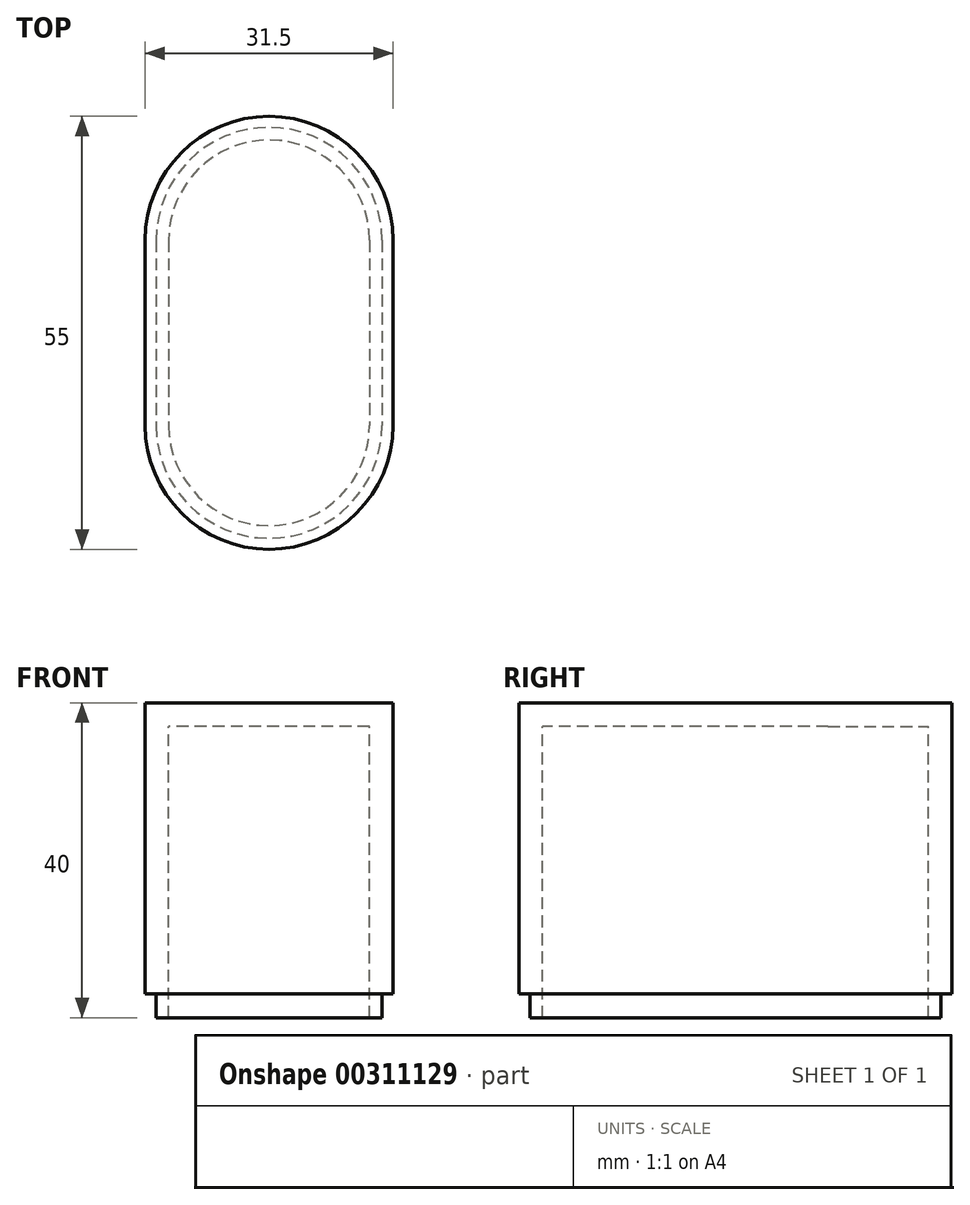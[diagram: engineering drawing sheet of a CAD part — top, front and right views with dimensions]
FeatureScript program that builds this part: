
annotation { "Feature Type Name" : "Feature", "Feature Type Description" : "" }
export const myFeature = defineFeature(function(context is Context, id is Id, definition is map)
    precondition{}
    {
        {
            var Q0;
            Q0=qCreatedBy(makeId("Top.planeOp"),FACE);
            var sketch = newSketch(context, id + "F0", { "sketchPlane" : qUnion([Q0])});
            skArc(sketch, "E0", {"start": v(12.75, 0) * mm, "mid": v(0, 12.75) * mm, "end": v(-12.75, 0) * mm});
            skLineSegment(sketch, "E1", {"start": v(12.75, 0) * mm, "end": v(12.75, 0) * mm});
            skLineSegment(sketch, "E2", {"start": v(-12.75, 0) * mm, "end": v(-12.75, -23.5) * mm});
            skLineSegment(sketch, "E3", {"start": v(-12.75, -23.5) * mm, "end": v(12.75, -23.5) * mm, "construction": true});
            skLineSegment(sketch, "E4", {"start": v(0, 0) * mm, "end": v(0, -23.5) * mm, "construction": true});
            skArc(sketch, "E5", {"start": v(-12.75, -23.5) * mm, "mid": v(0, -36.25) * mm, "end": v(12.75, -23.5) * mm});
            skLineSegment(sketch, "E6", {"start": v(12.75, 0) * mm, "end": v(12.75, -23.5) * mm});
            skArc(sketch, "E7.0", {"start": v(15.75, 0) * mm, "mid": v(0, 15.75) * mm, "end": v(-15.75, 0) * mm});
            skLineSegment(sketch, "E7.1", {"start": v(15.75, 0) * mm, "end": v(15.75, -23.5) * mm});
            skArc(sketch, "E7.2", {"start": v(-15.75, -23.5) * mm, "mid": v(0, -39.25) * mm, "end": v(15.75, -23.5) * mm});
            skLineSegment(sketch, "E7.3", {"start": v(-15.75, 0) * mm, "end": v(-15.75, -23.5) * mm});
            skCircle(sketch, "E8", {"center": v(0, 0) * mm, "radius": 12.75 * mm});
            skSolve(sketch);
        }
        {
            var Q0;
            Q0=qSketchRegion(id+"F0",true);
            var Q1;
            {var subQ0=sQuery(id+"F0.wireOp",EDGE,"E8");var subQ1=makeQuery(id+"F0.imprint","INTERSECT",VERTEX,{"derivedFrom":[sQuery(id+"F0.wireOp",EDGE,"E2"),subQ0]});Q1=makeQuery(id+"F0.imprint","IMPRINT",FACE,{"disambiguationData":[TD([[makeQuery(id+"F0.imprint","IMPRINT",EDGE,{"disambiguationData":[TD([[subQ1,1.0]])],"derivedFrom":subQ0}),1.0]])]});}
            var Q2;
            {var subQ0=sQuery(id+"F0.wireOp",EDGE,"E2");Q2=makeQuery(id+"F0.imprint","IMPRINT",FACE,{"disambiguationData":[TD([[makeQuery(id+"F0.imprint","IMPRINT",EDGE,{"derivedFrom":subQ0}),1.0]])]});}
            extrude(context, id + "F1", {"entities" : qUnion([Q0, Q1, Q2]), "depth" : 3 * mm});
        }
        {
            var Q0;
            {var subQ1=sQuery(id+"F0.wireOp",EDGE,"E2");Q0=makeQuery(id+"F0.imprint","IMPRINT",FACE,{"disambiguationData":[TD([[makeQuery(id+"F0.imprint","IMPRINT",EDGE,{"derivedFrom":subQ1}),-1.0]])]});}
            extrude(context, id + "F2", {"entities" : qUnion([Q0]), "operationType" : NewBodyOperationType.ADD, "oppositeDirection" : true, "depth" : 34 * mm});
        }
        {
            var Q0;
            Q0=makeQuery(id+"F2.opExtrude","CAP_FACE",FACE,{"disambiguationData":[OSD([sQuery(id+"F0.wireOp",EDGE,"E2"),sQuery(id+"F0.wireOp",EDGE,"E5"),sQuery(id+"F0.wireOp",EDGE,"E6"),sQuery(id+"F0.wireOp",EDGE,"E7.0"),sQuery(id+"F0.wireOp",EDGE,"E7.1"),sQuery(id+"F0.wireOp",EDGE,"E7.2"),sQuery(id+"F0.wireOp",EDGE,"E7.3"),sQuery(id+"F0.wireOp",EDGE,"E8")])],"isStart":false});
            var sketch = newSketch(context, id + "F3", { "sketchPlane" : qUnion([Q0])});
            skArc(sketch, "E9.0", {"start": v(-14.35, 23.5) * mm, "mid": v(0, 37.85) * mm, "end": v(14.35, 23.5) * mm});
            skLineSegment(sketch, "E9.1", {"start": v(-14.35, 0) * mm, "end": v(-14.35, 23.5) * mm});
            skArc(sketch, "E9.2", {"start": v(14.35, 0) * mm, "mid": v(0, -14.35) * mm, "end": v(-14.35, 0) * mm});
            skLineSegment(sketch, "E9.3", {"start": v(14.35, 0) * mm, "end": v(14.35, 23.5) * mm});
            skSolve(sketch);
        }
        {
            var Q0;
            Q0=makeQuery(id+"F3.imprint","IMPRINT",FACE,{"disambiguationData":[TD([[makeQuery(id+"F3.imprint","IMPRINT",EDGE,{"derivedFrom":sQuery(id+"F3.wireOp",EDGE,"E9.0")}),1.0]])]});
            extrude(context, id + "F4", {"entities" : qUnion([Q0]), "operationType" : NewBodyOperationType.ADD, "depth" : 3 * mm});
        }
    });
